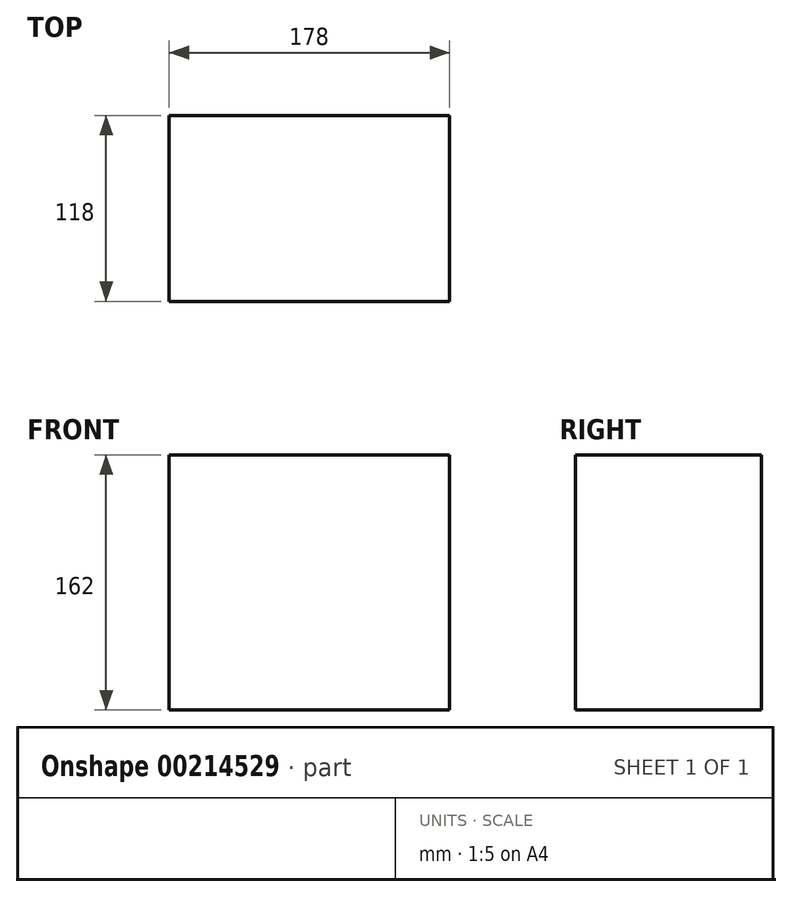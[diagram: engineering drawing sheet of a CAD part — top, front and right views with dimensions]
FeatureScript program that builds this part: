
annotation { "Feature Type Name" : "Feature", "Feature Type Description" : "" }
export const myFeature = defineFeature(function(context is Context, id is Id, definition is map)
    precondition{}
    {
        {
            var Q0;
            Q0=qCreatedBy(makeId("Front.planeOp"),FACE);
            var sketch = newSketch(context, id + "F0", { "sketchPlane" : qUnion([Q0])});
            skLineSegment(sketch, "E0.bottom", {"start": v(-89, 81) * mm, "end": v(89, 81) * mm});
            skLineSegment(sketch, "E0.top", {"start": v(-89, -81) * mm, "end": v(89, -81) * mm});
            skLineSegment(sketch, "E0.left", {"start": v(-89, 81) * mm, "end": v(-89, -81) * mm});
            skLineSegment(sketch, "E0.right", {"start": v(89, 81) * mm, "end": v(89, -81) * mm});
            skSolve(sketch);
        }
        {
            var Q0;
            Q0 = qSketchRegion(id + "F0", true);
            extrude(context, id + "F1", {"entities" : qUnion([Q0]), "depth" : 118 * mm});
        }
    });
